# Revit family: Sarlam_Eclairage_Borne_Chartres_Infini_T1_Anti_Vandale_Diam_322mm_2000Lm
name_source: partatom
category: Luminaires
units: mm (PartAtom-declared; Revit-internal decimal feet)

## family parameters
Basée sur le plan de construction = Non
Cote de connecteur circulaire = Utiliser le diamètre
Couper avec des vides une fois chargée = Non
Partagée = Non
Point de calcul de pièce = Non
Source d'éclairage = Non
Toujours verticalement = Oui
Type d'élément = Normal

## types (28) — shared parameters
Angle du faisceau = Faisceau libre
Appareillage = Appareil à LED commandé en courant
Classe de protection = II
Condition Générale d'Utilisation = https://export.legrand.com
Diamètre externe = 322 mm  [stored 1.05643 ft]
Douille = Sans
Fabricant = LEGRAND
Flux lumineux utile lm = 2000
Hauteur/profondeur = 70 mm  [stored 0.229659 ft]
Indice de rendu des couleurs CRI = 80-89
Largeur = 322 mm  [stored 1.05643 ft]
Longueur = 322 mm  [stored 1.05643 ft]
Matériau du boîtier/corps = Plastique
Puissance de la lampe en Multiwatt = 21/39W
Répartition lumineuse = Symétrique
Source lumineuse = Led non interchangeable
Température de couleur K MAX = 4000
Température de couleur K MIN = 4000
Tension nominale (Un) V MAX = 253
Tension nominale (Un) V MIN = 207
Type de tension = CA
URL = http://www.legrandoc.com
URL Hublot = http://www.legrandoc.com
zero-valued in all types: Elévation par défaut

## per-type parameters (varying)
| type | Avec détecteur crépusculaire | Avec détecteur de mouvement | Couleur du boîtier/corps | Courant nominal mA MAX | Courant nominal mA MIN | Description | Hauteur borne | Hauteur pieds | Hublot | Indice de protection (IP) | Indice de protection contre les chocs (IK) | Modèle | Puissance du système W | Type de variation |
| Borne 600 + ON/OFF BLANC | Non | Non | LEGRAND - Blanc | 131 | 106 | BORNE CHARTRES INFINI HAUTEUR 600 + CHARTRES INFINI 2000LM 4000K AV ON/OFF BLANC | 600 mm | 524 mm | Legrand-Eclairage-Hublot-Chartres Infini-T1 Anti Vandale Diam 322mm-2000Lm : ON/OFF BLANC | IP55 | IK10 | SL-532030 + SL-532024 | 27 | Non régulable |
| Borne 1200 + ON/OFF BLANC | Non | Non | LEGRAND - Blanc | 131 | 106 | BORNE CHARTRES INFINI HAUTEUR 1200 + CHARTRES INFINI 2000LM 4000K AV ON/OFF BLANC | 1200 mm | 1124 mm  [stored 3.68766 ft] | Legrand-Eclairage-Hublot-Chartres Infini-T1 Anti Vandale Diam 322mm-2000Lm : ON/OFF BLANC | IP55 | IK10 | SL-532033 + SL-532024 | 27 | Non régulable |
| Borne 600 + ON/OFF ANTHRACITE | Non | Non | LEGRAND - Anthracite | 131 | 106 | BORNE CHARTRES INFINI HAUTEUR 600 + CHARTRES INFINI 2000LM 4000K AV ON/OFF ANTHRACITE | 600 mm | 524 mm | Legrand-Eclairage-Hublot-Chartres Infini-T1 Anti Vandale Diam 322mm-2000Lm : ON/OFF ANTHRACITE | IP55 | IK10 | SL-532031 + SL-532025 | 27 | Non régulable |
| Borne 1200 + ON/OFF ANTHRACITE | Non | Non | LEGRAND - Anthracite | 131 | 106 | BORNE CHARTRES INFINI HAUTEUR 1200 + CHARTRES INFINI 2000LM 4000K AV ON/OFF ANTHRACITE | 1200 mm | 1124 mm  [stored 3.68766 ft] | Legrand-Eclairage-Hublot-Chartres Infini-T1 Anti Vandale Diam 322mm-2000Lm : ON/OFF ANTHRACITE | IP55 | IK10 | SL-532034 + SL-532025 | 27 | Non régulable |
| Borne 600 + ON/OFF GRIS METAL | Non | Non | LEGRAND - Gris métal | 131 | 106 | BORNE CHARTRES INFINI HAUTEUR 600 + CHARTRES INFINI 2000LM 4000K AV ON/OFF GRIS METAL | 600 mm | 524 mm | Legrand-Eclairage-Hublot-Chartres Infini-T1 Anti Vandale Diam 322mm-2000Lm : ON/OFF GRIS METAL | IP55 | IK10 | SL-532032 + SL-532026 | 27 | Non régulable |
| Borne 1200 + ON/OFF GRIS METAL | Non | Non | LEGRAND - Gris métal | 131 | 106 | BORNE CHARTRES INFINI HAUTEUR 1200 + CHARTRES INFINI 2000LM 4000K STANDARD ON/OFF GRIS METAL | 1200 mm | 1124 mm  [stored 3.68766 ft] | Legrand-Eclairage-Hublot-Chartres Infini-T1 Anti Vandale Diam 322mm-2000Lm : ON/OFF GRIS METAL | IP55 | IK10 | SL-532035 + SL-532026 | 27 | Non régulable |
| Borne 600 + Détection BLANC | Oui | Oui | LEGRAND - Blanc | 135 | 110 | BORNE CHARTRES INFINI HAUTEUR 600 + CHARTRES INFINI 2000LM 4000K AV DETECTION HF BLANC | 600 mm | 524 mm | Legrand-Eclairage-Hublot-Chartres Infini-T1 Anti Vandale Diam 322mm-2000Lm : Détection BLANC | IP55 | IK10 | SL-532030 + SL-532064 | 28 | Autre |
| Borne 1200 + Détection BLANC | Oui | Oui | LEGRAND - Blanc | 135 | 110 | BORNE CHARTRES INFINI HAUTEUR 1200 + CHARTRES INFINI 2000LM 4000K AV DETECTION HF BLANC | 1200 mm | 1124 mm  [stored 3.68766 ft] | Legrand-Eclairage-Hublot-Chartres Infini-T1 Anti Vandale Diam 322mm-2000Lm : Détection BLANC | IP55 | IK10 | SL-532033 + SL-532064 | 28 | Autre |
| Borne 600 + Détection ANTHRACITE | Oui | Oui | LEGRAND - Anthracite | 135 | 110 | BORNE CHARTRES INFINI HAUTEUR 600 + CHARTRES INFINI 2000LM 4000K AV DETECTION HF ANTHRACITE | 600 mm | 524 mm | Legrand-Eclairage-Hublot-Chartres Infini-T1 Anti Vandale Diam 322mm-2000Lm : Détection ANTHRACITE | IP55 | IK10 | SL-532031 + SL-532065 | 28 | Autre |
| Borne 1200 + Détection ANTHRACITE | Oui | Oui | LEGRAND - Anthracite | 135 | 110 | BORNE CHARTRES INFINI HAUTEUR 1200 + CHARTRES INFINI 2000LM 4000K AV DETECTION HF ANTHRACITE | 1200 mm | 1124 mm  [stored 3.68766 ft] | Legrand-Eclairage-Hublot-Chartres Infini-T1 Anti Vandale Diam 322mm-2000Lm : Détection ANTHRACITE | IP55 | IK10 | SL-532034 + SL-532065 | 28 | Autre |
| Borne 600 + Détection GRIS METAL | Oui | Oui | LEGRAND - Gris métal | 135 | 110 | BORNE CHARTRES INFINI HAUTEUR 600 + CHARTRES INFINI 2000LM 4000K AV DETECTION HF GRIS METAL | 600 mm | 524 mm | Legrand-Eclairage-Hublot-Chartres Infini-T1 Anti Vandale Diam 322mm-2000Lm : Détection GRIS METAL | IP55 | IK10 | SL-532032 + SL-532066 | 28 | Autre |
| Borne 1200 + Détection GRIS METAL | Oui | Oui | LEGRAND - Gris métal | 135 | 110 | BORNE CHARTRES INFINI HAUTEUR 1200 + CHARTRES INFINI 2000LM 4000K AV DETECTION HF GRIS METAL | 1200 mm | 1124 mm  [stored 3.68766 ft] | Legrand-Eclairage-Hublot-Chartres Infini-T1 Anti Vandale Diam 322mm-2000Lm : Détection GRIS METAL | IP55 | IK10 | SL-532035 + SL-532066 | 28 | Autre |
| Borne 600 + Détection+Horloge BLANC | Oui | Oui | LEGRAND - Blanc | 135 | 110 | BORNE CHARTRES INFINI HAUTEUR 600 + CHARTRES INFINI 2000LM 4000K  AV DETECTION HF + HORLOGE BLANC | 600 mm | 524 mm | Legrand-Eclairage-Hublot-Chartres Infini-T1 Anti Vandale Diam 322mm-2000Lm : Détection+Horloge BLANC | IP55 | IK10 | SL-532030 + SL-532079 | 28 | Autre |
| Borne 1200 + Détection+Horloge BLANC | Oui | Oui | LEGRAND - Blanc | 135 | 110 | BORNE CHARTRES INFINI HAUTEUR 1200 + CHARTRES INFINI 2000LM 4000K  AV DETECTION HF + HORLOGE BLANC | 1200 mm | 1124 mm  [stored 3.68766 ft] | Legrand-Eclairage-Hublot-Chartres Infini-T1 Anti Vandale Diam 322mm-2000Lm : Détection+Horloge BLANC | IP55 | IK10 | SL-532033 + SL-532079 | 28 | Autre |
| Borne 600 + Détection+Horloge ANTHRACITE | Oui | Oui | LEGRAND - Anthracite | 135 | 110 | BORNE CHARTRES INFINI HAUTEUR 600 + CHARTRES INFINI 2000LM 4000K  AV DETECTION HF + HORLOGE ANTRACITE | 600 mm | 524 mm | Legrand-Eclairage-Hublot-Chartres Infini-T1 Anti Vandale Diam 322mm-2000Lm : Détection+Horloge ANTHRACITE | IP55 | IK10 | SL-532031 + SL-532080 | 28 | Autre |
| Borne 1200 + Détection+Horloge ANTHRACITE | Oui | Oui | LEGRAND - Anthracite | 135 | 110 | BORNE CHARTRES INFINI HAUTEUR 1200 + CHARTRES INFINI 2000LM 4000K  AV DETECTION HF + HORLOGE ANTRACITE | 1200 mm | 1124 mm  [stored 3.68766 ft] | Legrand-Eclairage-Hublot-Chartres Infini-T1 Anti Vandale Diam 322mm-2000Lm : Détection+Horloge ANTHRACITE | IP55 | IK10 | SL-532034 + SL-532080 | 28 | Autre |
| Borne 600 + Détection+Horloge GRIS METAL | Oui | Oui | LEGRAND - Gris métal | 135 | 110 | BORNE CHARTRES INFINI HAUTEUR 600 + CHARTRES INFINI 2000LM 4000K  AV DETECTION HF + HORLOGE GRIS METAL | 600 mm | 524 mm | Legrand-Eclairage-Hublot-Chartres Infini-T1 Anti Vandale Diam 322mm-2000Lm : Détection+Horloge GRIS METAL | IP55 | IK10 | SL-532032 + SL-532081 | 28 | Autre |
| Borne 1200 + Détection+Horloge GRIS METAL | Oui | Oui | LEGRAND - Gris métal | 135 | 110 | BORNE CHARTRES INFINI HAUTEUR 1200 + CHARTRES INFINI 2000LM 4000K  AV DETECTION HF + HORLOGE GRIS METAL | 1200 mm | 1124 mm  [stored 3.68766 ft] | Legrand-Eclairage-Hublot-Chartres Infini-T1 Anti Vandale Diam 322mm-2000Lm : Détection+Horloge GRIS METAL | IP55 | IK10 | SL-532035 + SL-532081 | 28 | Autre |
| Borne 600 + Double niveau/Minuterie BLANC | Non | Non | LEGRAND - Blanc | 135 | 110 | BORNE CHARTRES INFINI HAUTEUR 600 + CHARTRES INFINI 2000LM 4000K STD DOUBLE NIVEAU/MINUTERIE BLANC | 600 mm | 524 mm | Legrand-Eclairage-Hublot-Chartres Infini-T1 Anti Vandale Diam 322mm-2000Lm : Double niveau/Minuterie BLANC | IP55 | IK10 | SL-532030 + SL-532090 | 28 | Autre |
| Borne 1200 + Double niveau/Minuterie BLANC | Non | Non | LEGRAND - Blanc | 135 | 110 | BORNE CHARTRES INFINI HAUTEUR 1200 + CHARTRES INFINI 2000LM 4000K AV DOUBLE NIVEAU/MINUTERIE BLANC | 1200 mm | 1124 mm  [stored 3.68766 ft] | Legrand-Eclairage-Hublot-Chartres Infini-T1 Anti Vandale Diam 322mm-2000Lm : Double niveau/Minuterie BLANC | IP55 | IK10 | SL-532033 + SL-532090 | 28 | Autre |
| Borne 600 + Double niveau/Minuterie ANTRACITE | Non | Non | LEGRAND - Anthracite | 135 | 110 | BORNE CHARTRES INFINI HAUTEUR 600 + CHARTRES INFINI 2000LM 4000K STD DOUBLE NIVEAU/MINUTERIE ANTHRACITE | 600 mm | 524 mm | Legrand-Eclairage-Hublot-Chartres Infini-T1 Anti Vandale Diam 322mm-2000Lm : Double niveau/Minuterie ANTHRACITE | IP55 | IK10 | SL-532031 + SL-532091 | 28 | Autre |
| Borne 1200 + Double niveau/Minuterie ANTHRACITE | Non | Non | LEGRAND - Anthracite | 135 | 110 | BORNE CHARTRES INFINI HAUTEUR 1200 + CHARTRES INFINI 2000LM 4000K AV DOUBLE NIVEAU/MINUTERIE ANTHRACITE | 1200 mm | 1124 mm  [stored 3.68766 ft] | Legrand-Eclairage-Hublot-Chartres Infini-T1 Anti Vandale Diam 322mm-2000Lm : Double niveau/Minuterie ANTHRACITE | IP55 | IK10 | SL-532034 + SL-532091 | 28 | Autre |
| Borne 600 + Double niveau/Minuterie GRIS METAL | Non | Non | LEGRAND - Gris métal | 135 | 110 | BORNE CHARTRES INFINI HAUTEUR 600 + CHARTRES INFINI 2000LM 4000K AV DOUBLE NIVEAU/MINUTERIE GRIS METAL | 600 mm | 524 mm | Legrand-Eclairage-Hublot-Chartres Infini-T1 Anti Vandale Diam 322mm-2000Lm : Double niveau/Minuterie GRIS METAL | IP55 | IK10 | SL-532032 + SL-532092 | 28 | Autre |
| Borne 1200 + Double niveau/Minuterie GRIS METAL | Non | Non | LEGRAND - Gris métal | 135 | 110 | BORNE CHARTRES INFINI HAUTEUR 1200 + CHARTRES INFINI 2000LM 4000K AV DOUBLE NIVEAU/MINUTERIE GRIS METAL | 1200 mm | 1124 mm  [stored 3.68766 ft] | Legrand-Eclairage-Hublot-Chartres Infini-T1 Anti Vandale Diam 322mm-2000Lm : Double niveau/Minuterie GRIS METAL | IP55 | IK10 | SL-532035 + SL-532092 | 28 | Autre |
| Borne 1200 + Renforcé Détection | Oui | Oui | LEGRAND - Blanc | 135 | 110 | BORNE CHARTRES INFINI HAUTEUR 1200 + CHARTRES INFINI 2000LM 4000K SOLIROC DETECTION HF BLANC | 1200 mm | 1124 mm  [stored 3.68766 ft] | Legrand-Eclairage-Hublot-Chartres Infini-T1 Anti Vandale Diam 322mm-2000Lm : Renforcé-Détection | IP66 | >IK10 | SL-532033 + SL-532097 | 27 | Non régulable |
| Borne 600 + Renforcé Détection | Oui | Oui | LEGRAND - Blanc | 135 | 110 | BORNE CHARTRES INFINI HAUTEUR 600 + CHARTRES INFINI 2000LM 4000K SOLIROC DETECTION HF BLANC | 600 mm | 524 mm | Legrand-Eclairage-Hublot-Chartres Infini-T1 Anti Vandale Diam 322mm-2000Lm : Renforcé-Détection | IP66 | >IK10 | SL-532030 + SL-532097 | 28 | Autre |
| Borne 1200 + Renforcé ON/OFF | Non | Non | LEGRAND - Blanc | 135 | 110 | BORNE CHARTRES INFINI HAUTEUR 1200 + CHARTRES INFINI 2000LM 4000K SOLIROC ON/OFF BLANC | 1200 mm | 1124 mm  [stored 3.68766 ft] | Legrand-Eclairage-Hublot-Chartres Infini-T1 Anti Vandale Diam 322mm-2000Lm : Renforcé-ON/OFF | IP66 | >IK10 | SL-532033 + SL-532096 | 27 | Non régulable |
| Borne 600 + Renforcé ON/OFF | Non | Non | LEGRAND - Blanc | 135 | 110 | BORNE CHARTRES INFINI HAUTEUR 600 + CHARTRES INFINI 2000LM 4000K SOLIROC ON/OFF BLANC | 600 mm | 524 mm | Legrand-Eclairage-Hublot-Chartres Infini-T1 Anti Vandale Diam 322mm-2000Lm : Renforcé-ON/OFF | IP66 | >IK10 | SL-532030 + SL-532096 | 27 | Non régulable |

note: [stored X ft] marks values corroborated as IEEE doubles in the binary element streams (Revit-internal decimal feet)

## geometry (parser evidence)
native form markers: Blend x14
no freeform markers — native parametric forms only
